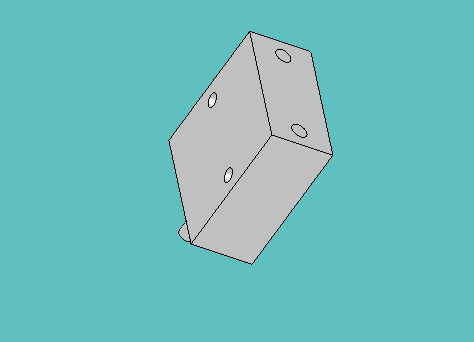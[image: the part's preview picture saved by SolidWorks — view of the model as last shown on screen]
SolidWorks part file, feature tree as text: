
SOLIDWORKS PART (.sldprt)
format: sldprt  version: not decoded by parser v0  size: 366,592 bytes
history: native  units: mm
features: sketch x4, extrude x3, material x1, boolean_combine x1, cut_extrude x1 (+11 scaffold rows collapsed)
feature tree (21):
  scaffold x11  (default folders/planes/origin — collapsed)
  material  "Material <not specified>"
  sketch  "Sketch3"  dims[c1.D2=2.794mm c1.D4=2.794mm c1.D1=27.0256mm c2.D2=9.9822mm c2.D3=28.575mm c2.D5=14.2748mm c2.D6=14.2748mm c2.D7=9.779mm c2.D8=9.779mm c2.D9=9.9822mm]
  extrude  "Extrude3"  Depth=12.7mm
  sketch  "Sketch5"  dims[D2=2.9972mm D1=6.35mm]
  extrude  "Extrude4"  Depth=8.73125mm
  sketch  "Sketch9"  dims[D1=3.175mm D2=~1.731942mm D3=~6.848039mm D4=9.779mm]
  extrude  "Extrude8"  Depth=7.14375mm
  boolean_combine  "Combine5"
  sketch  "Sketch10"
  cut_extrude  "Cut-Extrude1"  Depth=7.14375mm
decode coverage: 7 of 9 modeling features carry decoded parameters
note: ~ marks probable driven/reference dimensions
note: suppression state not decoded; provenance and decode notes live in map.json
